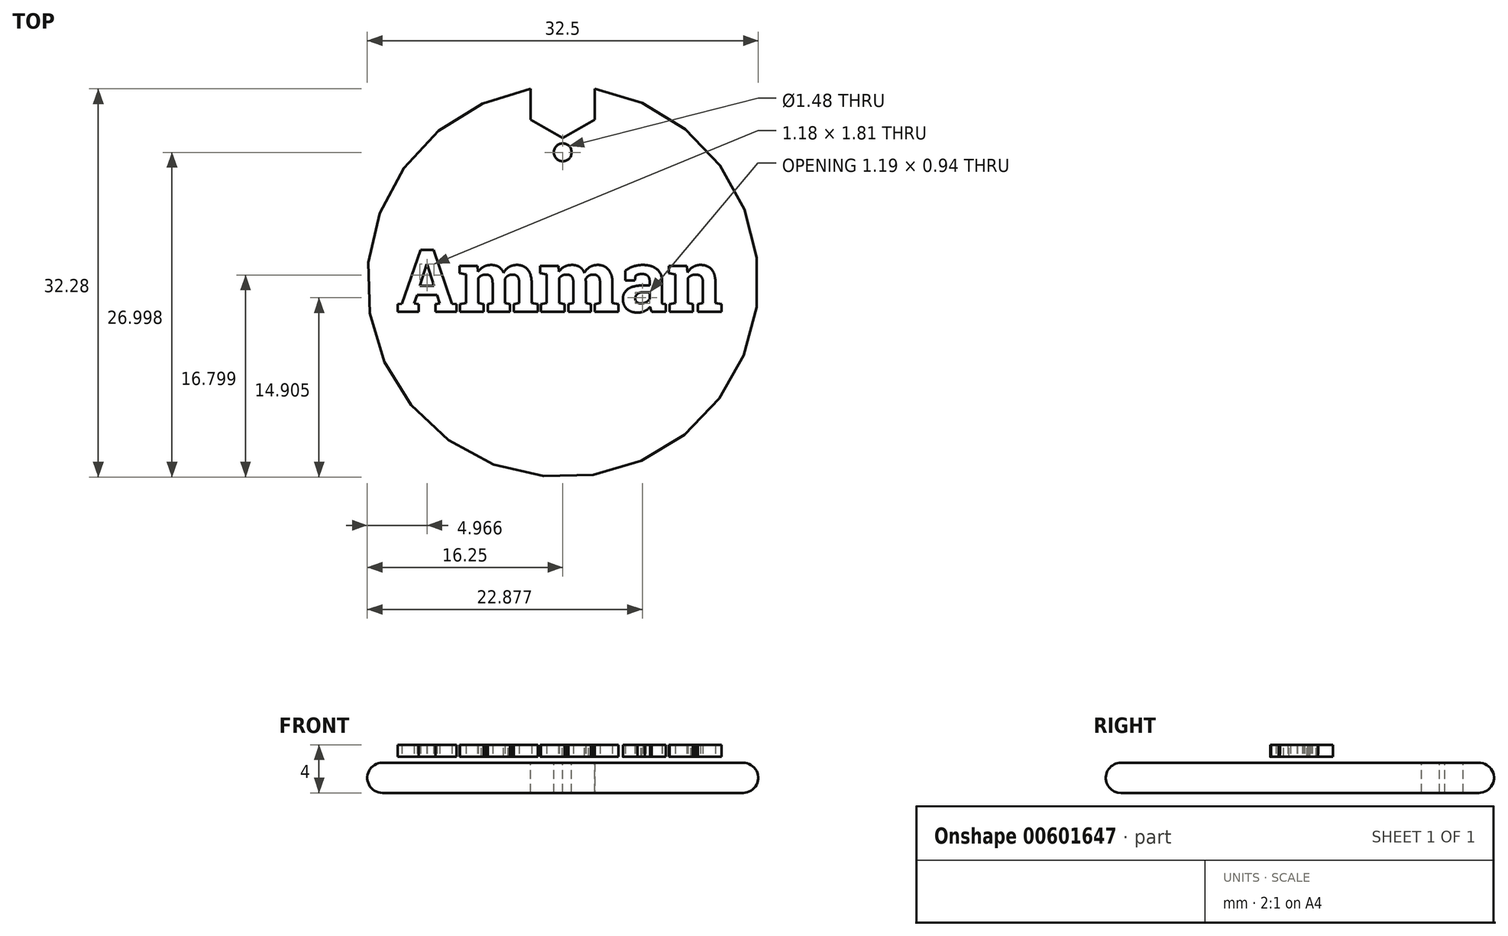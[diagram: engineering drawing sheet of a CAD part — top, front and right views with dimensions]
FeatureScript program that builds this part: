
annotation { "Feature Type Name" : "Feature", "Feature Type Description" : "" }
export const myFeature = defineFeature(function(context is Context, id is Id, definition is map)
    precondition{}
    {
        {
            var Q0;
            Q0=qCreatedBy(makeId("Front.planeOp"),FACE);
            var sketch = newSketch(context, id + "F0", { "sketchPlane" : qUnion([Q0])});
            skLineSegment(sketch, "E0.bottom", {"start": v(0, 0) * mm, "end": v(-15, 0) * mm});
            skLineSegment(sketch, "E0.top", {"start": v(0, 2.5) * mm, "end": v(-15, 2.5) * mm});
            skLineSegment(sketch, "E0.left", {"start": v(0, 0) * mm, "end": v(0, 2.5) * mm});
            skLineSegment(sketch, "E0.right", {"start": v(-15, 0) * mm, "end": v(-15, 2.5) * mm});
            skArc(sketch, "E1", {"start": v(-15, 2.5) * mm, "mid": v(-16.25, 1.25) * mm, "end": v(-15, 0) * mm});
            skSolve(sketch);
        }
        {
            var Q0;
            Q0 = qSketchRegion(id + "F0", true);
            var Q1;
            Q1=sQuery(id+"F0.wireOp",EDGE,"E0.left");
            revolve(context, id + "F1", {"entities" : qUnion([Q0]), "axis" : qUnion([Q1]), "revolveType" : RevolveType.FULL});
        }
        {
            var Q0;
            Q0=qCreatedBy(makeId("Top.planeOp"),FACE);
            cPlane(context, id + "F2", {"entities" : qUnion([Q0]), "cplaneType" : CPlaneType.OFFSET, "offset" : 3 * mm, "width" : 152.4 * mm, "height" : 152.4 * mm});
        }
        {
            var Q0;
            Q0=qCreatedBy(id+"F2.planeOp",FACE);
            var sketch = newSketch(context, id + "F3", { "sketchPlane" : qUnion([Q0])});
            skText(sketch, "E2", { "text": "Amman", "fontName": "RobotoSlab-Bold.ttf"});
            const initialGuessF3  = {"E2": [-0.01388, -0.0025, 1, 0, 0.0052]};
            skSetInitialGuess(sketch, initialGuessF3);
            skSolve(sketch);
        }
        {
            var Q0;
            Q0 = qSketchRegion(id + "F3", true);
            extrude(context, id + "F4", {"entities" : qUnion([Q0]), "depth" : 1 * mm, "offsetDistance" : 25.4 * mm});
        }
        {
            var Q0;
            Q0=makeQuery(id+"F1.opRevolve","SWEPT_FACE",FACE,{"disambiguationData":[OSD([sQuery(id+"F0.wireOp",EDGE,"E0.top")])]});
            var sketch = newSketch(context, id + "F5", { "sketchPlane" : qUnion([Q0])});
            skCircle(sketch, "E3.cCircle", {"center": v(0, 15) * mm, "radius": 2.66 * mm, "construction": true});
            skLineSegment(sketch, "E3.0", {"start": v(2.66, 16.54) * mm, "end": v(2.66, 13.46) * mm});
            skLineSegment(sketch, "E3.1", {"start": v(2.66, 13.46) * mm, "end": v(0, 11.93) * mm});
            skLineSegment(sketch, "E3.2", {"start": v(0, 11.93) * mm, "end": v(-2.66, 13.46) * mm});
            skLineSegment(sketch, "E3.3", {"start": v(-2.66, 13.46) * mm, "end": v(-2.66, 16.54) * mm});
            skLineSegment(sketch, "E3.4", {"start": v(-2.66, 16.54) * mm, "end": v(0, 18.07) * mm});
            skLineSegment(sketch, "E3.5", {"start": v(0, 18.07) * mm, "end": v(2.66, 16.54) * mm});
            skPoint(sketch, "E3.0.midPoint", {"position": v(2.66, 15) * mm});
            skSolve(sketch);
        }
        {
            var Q0;
            Q0 = qSketchRegion(id + "F5", true);
            extrude(context, id + "F6", {"entities" : qUnion([Q0]), "operationType" : NewBodyOperationType.REMOVE, "oppositeDirection" : true, "depth" : 25.4 * mm, "offsetDistance" : 25.4 * mm});
        }
        {
            var Q0;
            Q0=makeQuery(id+"F1.opRevolve","SWEPT_FACE",FACE,{"disambiguationData":[OSD([sQuery(id+"F0.wireOp",EDGE,"E0.top")])]});
            var sketch = newSketch(context, id + "F7", { "sketchPlane" : qUnion([Q0])});
            skCircle(sketch, "E4", {"center": v(0, 10.75) * mm, "radius": 0.74 * mm});
            skSolve(sketch);
        }
        {
            var Q0;
            Q0 = qSketchRegion(id + "F7", true);
            extrude(context, id + "F8", {"entities" : qUnion([Q0]), "operationType" : NewBodyOperationType.REMOVE, "oppositeDirection" : true, "depth" : 25.4 * mm, "offsetDistance" : 25.4 * mm});
        }
    });
